# Revit family: WashbasinUnit-Vitra-ValarteSeries-62204+62205+62206+62207+62208+62209+62210+62211+62212
name_source: partatom
category: Furniture Systems
revit_build: Autodesk Revit 2017 (Build: 20160225_1515(x64)
units: mm (PartAtom-declared; Revit-internal decimal feet)

## family parameters
Cut with Voids When Loaded = No
Host = Face
OmniClass Number = 23.40.00.00
OmniClass Title = Equipment and Furnishings
Part Type = Normal
Room Calculation Point = No
Round Connector Dimension = Use Diameter
Shared = Yes

## types (9) — shared parameters
BIMobject category = Bathroom compound units
Construction Type = Face Mounted
Default Elevation = 660 mm
Depth(mm) = 520 mm  [stored 1.70604 ft]
Design country = Turkey
Height(mm) = 828 mm
IFC Classification = Furniture
Manufacturer = Vitra
Manufacturer name = Vitra
Masterformat 2014 Code = 13 42 13
Masterformat 2014 Description = Bathroom Unit Modules
NBS Referans Code = 35-75-08
NBS Referans Description = Bathroom Cabinets
Nominal height = 0.000
Nominal width = 0.000
OmniClass Code = 23-31 25 13
OmniClass Description = Bathroom Cabinets
Product certification = https://vitraglobal.com
Product data url = https://www.vitra.com.tr
Product family = Valarte
Product group = Washbasin Unit
Technical description = https://www.vitra.com.tr
UNSPSC Code = 301815
UNSPSC Description = Bathroom Cabinets
URL = https://vitraglobal.com
Uniclass 1.4 Code = L8241
Uniclass 1.4 Description = Bathroom Cabinets
Uniclass 2.0 Code = PR-35-75-08
Uniclass 2.0 Description = Bathroom Cabinets
Uniclass 2015 Code = Pr_40_20_93
Uniclass 2015 Name = Wash basins, sinks and troughs
Uniformat II Code = E20
Uniformat II Description = FURNISHINGS
Warranty Period (Year) = 2
Weight Net (kg) = 95
Width(mm) = 1495 mm
Youtube = https://www.youtube.com

## per-type parameters (varying)
| type | Article No. (default) | Color | Description | Left | Model | Primary Material | Product SKU | Right |
| WashbasinUnit-Vitra-ValarteSeries-150cm-MatteWhite-Left_62204 | 62204 | Matte White | Valarte Washbasin Cabinet 150 cm, Double Drawer, Counter Top with Sink, Matt White, Left | No | 62204 | Vitra-MattWhite | 62204 | Yes |
| WashbasinUnit-Vitra-ValarteSeries-150cm-MatteGrey-Left_62205 | 62205 | Matte Grey | Valarte Washbasin Cabinet 150 cm, Double Drawer, Counter Top with Sink, Matt Grey, Left | No | 62205 | Vitra-MatteGrey | 62205 | Yes |
| WashbasinUnit-Vitra-ValarteSeries-150cm-MatteIvory-Left_62206 | 62206 | Matte Ivory | Valarte Washbasin Cabinet 150 cm, Double Drawer, Counter Top with Sink, Matt Ivory, Left | No | 62206 | Vitra-Matte Ivory | 62206 | Yes |
| WashbasinUnit-Vitra-ValarteSeries-150cm-MatteWhite-Right_62207 | 62207 | Matte White | Valarte Washbasin Cabinet 150 cm, Double Drawer, Counter Top with Sink, Matt White, Right | Yes | 62207 | Vitra-MattWhite | 62207 | No |
| WashbasinUnit-Vitra-ValarteSeries-150cm-MatteGrey-Right_62208 | 62208 | Matte Grey | Valarte Washbasin Cabinet 150 cm, Double Drawer, Counter Top with Sink, Matt Grey, Right | Yes | 62208 | Vitra-MatteGrey | 62208 | No |
| WashbasinUnit-Vitra-ValarteSeries-150cm-MatteIvory-Right_62209 | 62209 | Matte Ivory | Valarte Washbasin Cabinet 150 cm, Double Drawer, Counter Top with Sink, Matt Ivory, Right | Yes | 62209 | Vitra-Matte Ivory | 62209 | No |
| WashbasinUnit-Vitra-ValarteSeries-150cm-MatteWhite_62210 | 62210 | Matte White | Valarte Washbasin Cabinet 150 cm, Double Drawer, Counter Top Washbasin, Matt White, Double Washbasin | No | 62210 | Vitra-MattWhite | 62210 | No |
| WashbasinUnit-Vitra-ValarteSeries-150cm-MatteGrey_62211 | 62211 | Matte Grey | Valarte Washbasin Cabinet 150 cm, Double Drawer, Counter Top Washbasin, Matt Grey, Double Washbasin | No | 62211 | Vitra-MatteGrey | 62211 | No |
| WashbasinUnit-Vitra-ValarteSeries-150cm-MatteIvory_62212 | 62212 | Matte Ivory | Valarte Washbasin Cabinet 150 cm, Double Drawer, Counter Top Washbasin, Matt Ivory, Double Washbasin | No | 62212 | Vitra-Matte Ivory | 62212 | No |

note: [stored X ft] marks values corroborated as IEEE doubles in the binary element streams (Revit-internal decimal feet)

## geometry (parser evidence)
native form markers: Sweep x6
no freeform markers — native parametric forms only
